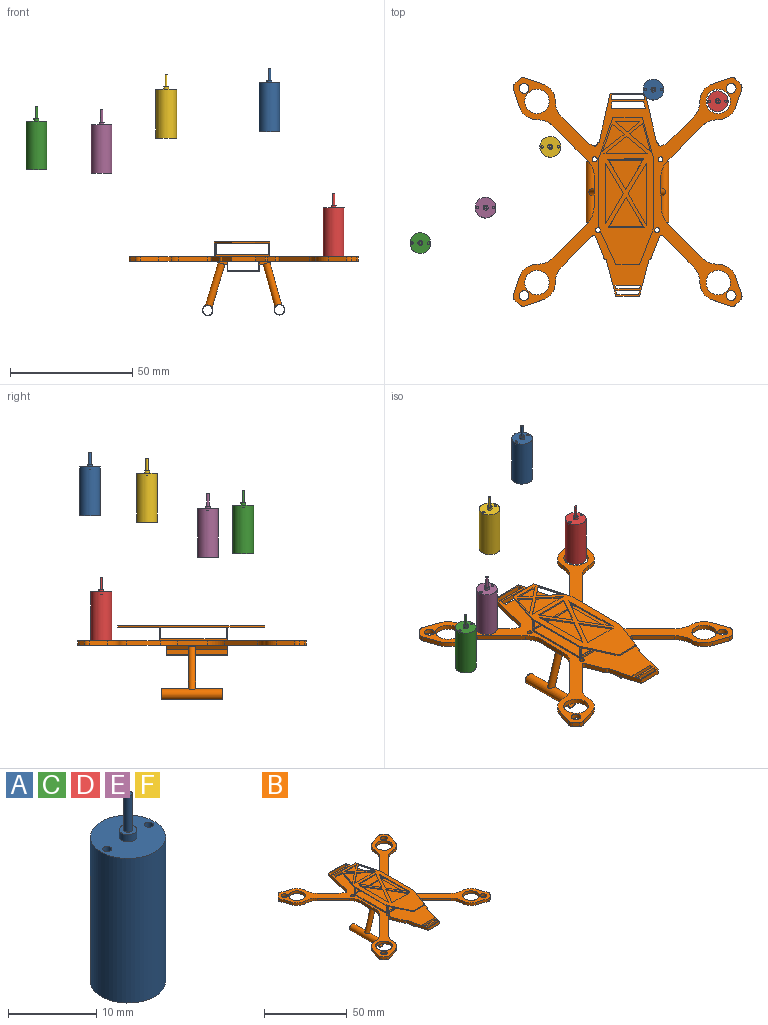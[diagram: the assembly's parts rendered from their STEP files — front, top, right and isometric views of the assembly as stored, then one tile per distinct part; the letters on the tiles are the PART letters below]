
ASSEMBLY  parts=6 mates=1
PART A: 11 faces, bbox 8.5x8.5x26 mm
  f0: plane 8.5x8.5mm, normal (0,0,1), area 52mm2, adj f1,f6,f7,f9
  f1: cylinder r=1mm len=2mm, axis (0,0,-1), area 6.3mm2, adj f0,f2
  f2: plane 2x2mm, normal (0,0,1), area 2.4mm2, adj f1,f3
  f3: cylinder r=0.5mm len=5mm, axis (0,0,-1), area 15.7mm2, adj f2,f4
  f4: plane 1x1mm, normal (0,0,1), area 0.8mm2, adj f3
  f5: plane 8.5x8.5mm, normal (0,0,-1), area 56.7mm2, adj f6
  f6: cylinder r=4.25mm len=20mm, axis (0,0,-1), area 534.1mm2, adj f0,f5
  f7: cylinder r=0.5mm len=1mm, axis (0,0,1), area 3.1mm2, adj f0,f8
  f8: plane 1x1mm, normal (0,0,1), area 0.8mm2, adj f7
  f9: cylinder r=0.5mm len=1mm, axis (0,0,1), area 3.1mm2, adj f0,f10
  f10: plane 1x1mm, normal (0,0,1), area 0.8mm2, adj f9
PART B: 207 faces, bbox 93.7x93.7x30.2 mm
  f0: plane 24.87x13.05mm, normal (0,0,-1), area 202.4mm2, adj f10,f122,f123,f124,f167,f168,f169,f170
  f1: plane 24.87x12.57mm, normal (0,0,1), area 190.7mm2, adj f10,f124,f125,f126,f167,f168,f169,f170
  f2: plane 60.16x22.71mm, normal (0,0,1), area 647.4mm2, adj f16,f18,f19,f20,f89,f103,f104,f105
  f3: plane 22.71x17.62mm, normal (0,0,-1), area 139.9mm2, adj f5,f18,f19,f20,f98,f99,f101,f103
  f4: plane 22.34x15.76mm, normal (0,0,-1), area 246.4mm2, adj f6,f16,f17,f21,f23,f105,f106,f143
  f5: plane 22.71x4.77mm, normal (0,-1,0), area 9.6mm2, adj f3,f7,f19,f20,f99,f100,f101,f102
  f6: plane 22.71x4.77mm, normal (0,1,0), area 9.6mm2, adj f4,f7,f19,f20,f21,f22,f23,f102
  f7: plane 26.78x22.71mm, normal (0,0,-1), area 259.4mm2, adj f5,f6,f19,f20,f143,f145,f146,f148
  f8: plane 93.73x93.73mm, normal (0,0,-1), area 2513.7mm2, adj f10,f11,f14,f15,f24,f25,f26,f27
  f9: plane 93.73x93.73mm, normal (0,0,1), area 2146.7mm2, adj f14,f15,f17,f19,f20,f24,f25,f26
  f10: plane 18.07x4mm, normal (0,-1,0), area 8.7mm2, adj f0,f1,f8,f11,f112,f122,f123,f125
  f11: plane 24.87x5.02mm, normal (-0.29,0,-0.96), area 123.4mm2, adj f8,f10,f13,f122,f124
  f12: cylinder r=1.5mm len=18.46mm, axis (-0.27,0,0.96), area 168.9mm2, adj f113,f117
  f13: cylinder r=1.5mm len=18.62mm, axis (0.29,0,0.96), area 170.6mm2, adj f11,f114
  f14: plane 14.44x2mm, normal (0,1,0), area 28.9mm2, adj f8,f9,f109,f110
  f15: plane 9.8x2mm, normal (0,-1,0), area 19.6mm2, adj f8,f9,f107,f108
  f16: plane 9.68x0.61mm, normal (0,-1,0), area 5.9mm2, adj f2,f4,f105,f106
  f17: plane 22.34x5.39mm, normal (0,-1,0), area 22.2mm2, adj f4,f9,f19,f21,f22,f23,f89
  f18: plane 12.03x0.61mm, normal (0,1,0), area 7.4mm2, adj f2,f3,f103,f104
  f19: plane 28.32x6mm, normal (1,0,0), area 41.4mm2, adj f2,f3,f5,f6,f7,f9,f17,f98
  f20: plane 28.07x6mm, normal (-1,0,0), area 40.6mm2, adj f2,f3,f5,f6,f7,f9,f89,f98
  f21: plane 4.58x0.76mm, normal (-1,0,0), area 3.5mm2, adj f4,f6,f17,f22
  f22: plane 21.4x0.76mm, normal (0,0,1), area 16.3mm2, adj f6,f17,f21,f23
  f23: plane 4.58x0.76mm, normal (1,0,0), area 3.5mm2, adj f4,f6,f17,f22
  f24: plane 7.46x2.53mm, normal (0.32,-0.95,0), area 15.8mm2, adj f8,f9,f25,f95
  f25: cylinder r=7.5mm len=7.1mm, axis (0,0,-1), area 18.7mm2, adj f8,f9,f24,f26
  f26: cylinder r=9.56mm len=6.75mm, axis (0,0,-1), area 15mm2, adj f8,f9,f25,f27
  f27: plane 12.22x12.22mm, normal (0.71,-0.71,0), area 34.6mm2, adj f8,f9,f26,f28
  f28: cylinder r=1mm len=2mm, axis (0,0,-1), area 4mm2, adj f8,f9,f27,f29
  f29: plane 8.48x3.23mm, normal (-0.93,-0.36,0), area 18.1mm2, adj f8,f9,f28,f30
  f30: cylinder r=1mm len=2mm, axis (0,0,-1), area 2.4mm2, adj f8,f9,f29,f107
  f31: cylinder r=1mm len=2mm, axis (0,0,-1), area 2.4mm2, adj f8,f9,f32,f108
  f32: plane 8.48x3.23mm, normal (0.93,-0.36,0), area 18.1mm2, adj f8,f9,f31,f33
  f33: cylinder r=1mm len=2mm, axis (0,0,-1), area 4mm2, adj f8,f9,f32,f34
  f34: plane 12.22x12.22mm, normal (-0.71,-0.71,0), area 34.6mm2, adj f8,f9,f33,f35
  f35: cylinder r=9.56mm len=6.75mm, axis (0,0,-1), area 15mm2, adj f8,f9,f34,f36
  f36: cylinder r=7.5mm len=7.1mm, axis (0,0,-1), area 18.7mm2, adj f8,f9,f35,f37
  f37: plane 7.46x2.53mm, normal (-0.32,-0.95,0), area 15.8mm2, adj f8,f9,f36,f38
  f38: cylinder r=2mm len=2.06mm, axis (0,0,-1), area 4.5mm2, adj f8,f9,f37,f39
  f39: plane 2.05x2.05mm, normal (0.71,-0.71,0), area 5.8mm2, adj f8,f9,f38,f40
  f40: cylinder r=2mm len=2.06mm, axis (0,0,-1), area 4.5mm2, adj f8,f9,f39,f41
  f41: plane 7.46x2.53mm, normal (0.95,0.32,0), area 15.8mm2, adj f8,f9,f40,f42
  f42: cylinder r=7.5mm len=7.1mm, axis (0,0,-1), area 18.7mm2, adj f8,f9,f41,f43
  f43: cylinder r=9.56mm len=6.75mm, axis (0,0,-1), area 15mm2, adj f8,f9,f42,f44
  f44: plane 13.69x13.69mm, normal (0.71,0.71,0), area 38.7mm2, adj f8,f9,f43,f45
  f45: cylinder r=10mm len=6.95mm, axis (0,0,-1), area 15.5mm2, adj f8,f9,f44,f46
  f46: plane 11.98x2mm, normal (1,0.01,0), area 24mm2, adj f8,f9,f45,f47
  f47: cylinder r=10mm len=7.2mm, axis (0,0,-1), area 16mm2, adj f8,f9,f46,f48
  f48: plane 13.85x13.85mm, normal (0.71,-0.71,0), area 39.2mm2, adj f8,f9,f47,f49
  f49: cylinder r=9.56mm len=6.75mm, axis (0,0,-1), area 15mm2, adj f8,f9,f48,f50
  f50: cylinder r=7.5mm len=7.1mm, axis (0,0,-1), area 18.7mm2, adj f8,f9,f49,f51
  f51: plane 7.46x2.53mm, normal (0.95,-0.32,0), area 15.8mm2, adj f8,f9,f50,f52
  f52: cylinder r=2mm len=2.06mm, axis (0,0,-1), area 4.5mm2, adj f8,f9,f51,f53
  f53: plane 2.05x2.05mm, normal (0.71,0.71,0), area 5.8mm2, adj f8,f9,f52,f54
  f54: cylinder r=2mm len=2.06mm, axis (0,0,-1), area 4.5mm2, adj f8,f9,f53,f55
  f55: plane 7.46x2.53mm, normal (-0.32,0.95,0), area 15.8mm2, adj f8,f9,f54,f56
  f56: cylinder r=7.5mm len=7.1mm, axis (0,0,-1), area 18.7mm2, adj f8,f9,f55,f57
  f57: cylinder r=9.56mm len=6.75mm, axis (0,0,-1), area 15mm2, adj f8,f9,f56,f58
  f58: plane 9.06x9.06mm, normal (-0.71,0.71,0), area 25.6mm2, adj f8,f9,f57,f59
  f59: cylinder r=10mm len=3.96mm, axis (0,0,-1), area 9.4mm2, adj f8,f9,f58,f60
  f60: cylinder r=1mm len=2mm, axis (0,0,-1), area 3.8mm2, adj f8,f9,f59,f61
  f61: cylinder r=0.78mm len=2mm, axis (0,0,-1), area 1.8mm2, adj f8,f9,f60,f109
  f62: cylinder r=0.78mm len=2mm, axis (0,0,-1), area 2.2mm2, adj f8,f9,f63,f110
  f63: cylinder r=1mm len=2mm, axis (0,0,-1), area 3.8mm2, adj f8,f9,f62,f64
  f64: cylinder r=10mm len=3.96mm, axis (0,0,-1), area 9.4mm2, adj f8,f9,f63,f65
  f65: plane 9.06x9.06mm, normal (0.71,0.71,0), area 25.6mm2, adj f8,f9,f64,f66
  f66: cylinder r=9.56mm len=6.75mm, axis (0,0,-1), area 15mm2, adj f8,f9,f65,f67
  f67: cylinder r=7.5mm len=7.1mm, axis (0,0,-1), area 18.7mm2, adj f8,f9,f66,f68
  f68: plane 7.46x2.53mm, normal (0.32,0.95,0), area 15.8mm2, adj f8,f9,f67,f69
  f69: cylinder r=2mm len=2.06mm, axis (0,0,-1), area 4.5mm2, adj f8,f9,f68,f70
  f70: plane 2.05x2.05mm, normal (-0.71,0.71,0), area 5.8mm2, adj f8,f9,f69,f71
  f71: cylinder r=2mm len=2.06mm, axis (0,0,-1), area 4.5mm2, adj f8,f9,f70,f72
  f72: plane 7.46x2.53mm, normal (-0.95,-0.32,0), area 15.8mm2, adj f8,f9,f71,f73
  f73: cylinder r=7.5mm len=7.1mm, axis (0,0,-1), area 18.7mm2, adj f8,f9,f72,f74
  f74: cylinder r=9.56mm len=6.75mm, axis (0,0,-1), area 15mm2, adj f8,f9,f73,f75
  f75: plane 13.85x13.85mm, normal (-0.71,-0.71,0), area 39.2mm2, adj f8,f9,f74,f76
  f76: cylinder r=10mm len=7.2mm, axis (0,0,-1), area 16mm2, adj f8,f9,f75,f77
  f77: plane 11.98x2mm, normal (-1,0.01,0), area 24mm2, adj f8,f9,f76,f78
  f78: cylinder r=10mm len=6.95mm, axis (0,0,-1), area 15.5mm2, adj f8,f9,f77,f79
  f79: plane 13.69x13.69mm, normal (-0.71,0.71,0), area 38.7mm2, adj f8,f9,f78,f80
  f80: cylinder r=9.56mm len=6.75mm, axis (0,0,-1), area 15mm2, adj f8,f9,f79,f81
  f81: cylinder r=7.5mm len=7.1mm, axis (0,0,-1), area 18.7mm2, adj f8,f9,f80,f82
  f82: plane 7.46x2.53mm, normal (-0.95,0.32,0), area 15.8mm2, adj f8,f9,f81,f83
  f83: cylinder r=2mm len=2.06mm, axis (0,0,-1), area 4.5mm2, adj f8,f9,f82,f84
  f84: plane 2.05x2.05mm, normal (-0.71,-0.71,0), area 5.8mm2, adj f8,f9,f83,f95
  f85: cylinder r=5mm len=10mm, axis (0,0,-1), area 62.8mm2, adj f8,f9
  f86: cylinder r=5mm len=10mm, axis (0,0,-1), area 62.8mm2, adj f8,f9
  f87: cylinder r=2mm len=4mm, axis (0,0,-1), area 25.1mm2, adj f8,f9
  f88: cylinder r=1mm len=2mm, axis (0,0,-1), area 12.6mm2, adj f8,f9
  f89: cylinder r=1mm len=8mm, axis (0,0,-1), area 14.9mm2, adj f2,f8,f9,f17,f20,f105
  f90: cylinder r=1mm len=2mm, axis (0,0,-1), area 12.6mm2, adj f8,f9
  f91: cylinder r=2mm len=4mm, axis (0,0,-1), area 25.1mm2, adj f8,f9
  f92: cylinder r=2mm len=4mm, axis (0,0,-1), area 25.1mm2, adj f8,f9
  f93: cylinder r=5mm len=10mm, axis (0,0,-1), area 62.8mm2, adj f8,f9
  f94: cylinder r=2mm len=4mm, axis (0,0,-1), area 25.1mm2, adj f8,f9
  f95: cylinder r=2mm len=2.06mm, axis (0,0,-1), area 4.5mm2, adj f8,f9,f24,f84
  f96: cylinder r=1mm len=2mm, axis (0,0,-1), area 12.6mm2, adj f8,f9
  f97: cylinder r=5mm len=10mm, axis (0,0,-1), area 62.8mm2, adj f8,f9
  f98: plane 22.71x5.39mm, normal (0,1,0), area 24.3mm2, adj f3,f9,f19,f20,f99,f100,f101
  f99: plane 4.58x0.62mm, normal (-1,0,0), area 2.8mm2, adj f3,f5,f98,f100
  f100: plane 21.4x0.62mm, normal (0,0,1), area 13.2mm2, adj f5,f98,f99,f101
  f101: plane 4.58x0.62mm, normal (1,0,0), area 2.8mm2, adj f3,f5,f98,f100
  f102: plane 26.78x22.71mm, normal (0,0,1), area 608.3mm2, adj f5,f6,f19,f20
  f103: plane 16.84x4.69mm, normal (0.96,0.27,0), area 10.7mm2, adj f2,f3,f18,f19
  f104: plane 16.98x6mm, normal (-0.94,0.33,0), area 11.1mm2, adj f2,f3,f18,f20
  f105: plane 15x6.85mm, normal (-0.91,-0.42,0), area 10.1mm2, adj f2,f4,f16,f89
  f106: plane 15x5.81mm, normal (0.93,-0.36,0), area 9.9mm2, adj f2,f4,f16,f19
  f107: plane 15x3.93mm, normal (-0.97,-0.25,0), area 31mm2, adj f8,f9,f15,f30
  f108: plane 15x3.89mm, normal (0.97,-0.25,0), area 31mm2, adj f8,f9,f15,f31
  f109: plane 20x4.56mm, normal (0.98,0.22,0), area 41mm2, adj f8,f9,f14,f61
  f110: plane 20x4.5mm, normal (-0.98,0.22,0), area 41mm2, adj f8,f9,f14,f62
  f111: plane 5.43x1.5mm, normal (0,-1,0), area 4.1mm2, adj f8,f112,f113
  f112: plane 1.5x0.12mm, normal (-1,0,0), area 0.2mm2, adj f8,f10,f111,f113
  f113: plane 24.99x5.43mm, normal (0.27,0,-0.96), area 133.8mm2, adj f8,f12,f111,f112,f123,f124
  f114: cylinder r=2.19mm len=25mm, axis (0,1,0), area 335.8mm2, adj f13,f115,f116
  f115: plane 4.37x4.37mm, normal (0,-1,0), area 2.4mm2, adj f114,f121
  f116: plane 4.37x4.37mm, normal (0,1,0), area 2.4mm2, adj f114,f121
  f117: cylinder r=2.19mm len=25mm, axis (0,1,0), area 335.7mm2, adj f12,f118,f119
  f118: plane 4.37x4.37mm, normal (0,-1,0), area 2.4mm2, adj f117,f120
  f119: plane 4.37x4.37mm, normal (0,1,0), area 2.4mm2, adj f117,f120
  f120: cylinder r=2mm len=25mm, axis (0,-1,0), area 314.8mm2, adj f118,f119
  f121: cylinder r=2mm len=25mm, axis (0,-1,0), area 314.1mm2, adj f115,f116
  f122: plane 24.87x2.5mm, normal (-1,0,0), area 62.2mm2, adj f0,f10,f11,f124
  f123: plane 24.87x2.5mm, normal (1,0,0), area 62.2mm2, adj f0,f10,f113,f124
  f124: plane 23.5x4mm, normal (0,1,0), area 12.8mm2, adj f0,f1,f8,f11,f113,f122,f123,f125
  f125: plane 24.87x3.76mm, normal (-1,0,0), area 93.4mm2, adj f1,f8,f10,f124
  f126: plane 24.87x3.76mm, normal (1,0,0), area 93.4mm2, adj f1,f8,f10,f124
  f127: plane 2.05x2mm, normal (0.98,-0.19,0), area 4.2mm2, adj f8,f9,f128,f130
  f128: plane 13.74x2mm, normal (0,1,0), area 27.5mm2, adj f8,f9,f127,f129
  f129: plane 2.05x2mm, normal (-0.98,-0.21,0), area 4.2mm2, adj f8,f9,f128,f130
  f130: plane 12.91x2mm, normal (0,-1,0), area 25.8mm2, adj f8,f9,f127,f129
  f131: plane 2.64x2mm, normal (0.99,-0.14,0), area 5.3mm2, adj f8,f9,f132,f134
  f132: plane 14.01x2mm, normal (0,1,0), area 28mm2, adj f8,f9,f131,f133
  f133: plane 2.64x2mm, normal (-0.97,-0.26,0), area 5.5mm2, adj f8,f9,f132,f134
  f134: plane 12.91x2mm, normal (0,-1,0), area 25.8mm2, adj f8,f9,f131,f133
  f135: plane 2x1.49mm, normal (-0.97,0.25,0), area 3.1mm2, adj f8,f9,f136,f138
  f136: plane 10.39x2mm, normal (0,-1,0), area 20.8mm2, adj f8,f9,f135,f137
  f137: plane 2x1.49mm, normal (0.97,0.25,0), area 3.1mm2, adj f8,f9,f136,f138
  f138: plane 9.61x2mm, normal (0,1,0), area 19.2mm2, adj f8,f9,f135,f137
  f139: plane 2x1.51mm, normal (-0.97,0.25,0), area 3.1mm2, adj f8,f9,f140,f142
  f140: plane 9.61x2mm, normal (0,-1,0), area 19.2mm2, adj f8,f9,f139,f141
  f141: plane 2x1.51mm, normal (0.97,0.25,0), area 3.1mm2, adj f8,f9,f140,f142
  f142: plane 8.83x2mm, normal (0,1,0), area 17.7mm2, adj f8,f9,f139,f141
  f143: plane 12.36x7.25mm, normal (0.86,-0.51,0), area 8.2mm2, adj f2,f4,f6,f7,f144,f145
  f144: plane 14.67x0.61mm, normal (0,1,0), area 9mm2, adj f2,f4,f143,f145
  f145: plane 12.44x7.42mm, normal (-0.86,-0.51,0), area 8.3mm2, adj f2,f4,f6,f7,f143,f144
  f146: plane 12.58x7.38mm, normal (-0.86,0.51,0), area 8.3mm2, adj f2,f3,f5,f7,f147,f148
  f147: plane 14.67x0.61mm, normal (0.01,-1,0), area 9mm2, adj f2,f3,f146,f148
  f148: plane 12.49x7.29mm, normal (0.86,0.5,0), area 8.2mm2, adj f2,f3,f5,f7,f146,f147
  f149: plane 12.6x7.39mm, normal (0.86,-0.51,0), area 8.3mm2, adj f2,f7,f150,f151
  f150: plane 12.93x7.55mm, normal (0.86,0.5,0), area 8.5mm2, adj f2,f7,f149,f151
  f151: plane 25.53x0.57mm, normal (-1,-0.01,0), area 14.5mm2, adj f2,f7,f149,f150
  f152: plane 12.36x7.25mm, normal (-0.86,0.51,0), area 8.1mm2, adj f2,f7,f153,f154
  f153: plane 12.4x7.4mm, normal (-0.86,-0.51,0), area 8.2mm2, adj f2,f7,f152,f154
  f154: plane 24.77x0.57mm, normal (1,0.01,0), area 14.1mm2, adj f2,f7,f152,f153
  f155: plane 4.93x4.12mm, normal (-0.64,-0.77,0), area 3.9mm2, adj f2,f3,f156,f157
  f156: plane 11.08x3.91mm, normal (0.94,-0.33,0), area 7.2mm2, adj f2,f3,f155,f157
  f157: plane 8.84x6.96mm, normal (-0.62,0.79,0), area 6.9mm2, adj f2,f3,f155,f156
  f158: plane 5.23x4.12mm, normal (-0.62,0.79,0), area 4.1mm2, adj f2,f3,f159,f160
  f159: plane 10.15x0.61mm, normal (0,-1,0), area 6.2mm2, adj f2,f3,f158,f160
  f160: plane 4.92x4.12mm, normal (0.64,0.77,0), area 3.9mm2, adj f2,f3,f158,f159
  f161: plane 8.65x7.24mm, normal (-0.64,-0.77,0), area 6.9mm2, adj f2,f3,f162,f163
  f162: plane 9.19x7.24mm, normal (0.62,-0.79,0), area 7.2mm2, adj f2,f3,f161,f163
  f163: plane 17.85x0.61mm, normal (0,1,0), area 11mm2, adj f2,f3,f161,f162
  f164: plane 5.44x4.28mm, normal (0.62,-0.79,0), area 4.3mm2, adj f2,f3,f165,f166
  f165: plane 8.64x7.23mm, normal (0.64,0.77,0), area 6.9mm2, adj f2,f3,f164,f166
  f166: plane 11.51x3.2mm, normal (-0.96,-0.27,0), area 7.3mm2, adj f2,f3,f164,f165
  f167: plane 3.03x0.24mm, normal (1,0,0), area 0.7mm2, adj f0,f1,f168,f170
  f168: plane 4.2x0.24mm, normal (0,-1,0), area 1mm2, adj f0,f1,f167,f169
  f169: plane 3.03x0.24mm, normal (-1,0,0), area 0.7mm2, adj f0,f1,f168,f170
  f170: plane 4.2x0.24mm, normal (0,1,0), area 1mm2, adj f0,f1,f167,f169
  f171: plane 3.85x0.24mm, normal (0,1,0), area 0.9mm2, adj f0,f1,f172,f174
  f172: plane 3.07x0.24mm, normal (1,0,0), area 0.7mm2, adj f0,f1,f171,f173
  f173: plane 3.85x0.24mm, normal (0,-1,0), area 0.9mm2, adj f0,f1,f172,f174
  f174: plane 3.07x0.24mm, normal (-1,0,0), area 0.7mm2, adj f0,f1,f171,f173
  f175: plane 4.2x0.24mm, normal (0,1,0), area 1mm2, adj f0,f1,f176,f178
  f176: plane 3.01x0.24mm, normal (1,0,0), area 0.7mm2, adj f0,f1,f175,f177
  f177: plane 4.2x0.24mm, normal (0,-1,0), area 1mm2, adj f0,f1,f176,f178
  f178: plane 3.01x0.24mm, normal (-1,0,0), area 0.7mm2, adj f0,f1,f175,f177
  f179: plane 3.85x0.24mm, normal (0,1,0), area 0.9mm2, adj f0,f1,f180,f182
  f180: plane 3.01x0.24mm, normal (1,0,0), area 0.7mm2, adj f0,f1,f179,f181
  f181: plane 3.85x0.24mm, normal (0,-1,0), area 0.9mm2, adj f0,f1,f180,f182
  f182: plane 3.01x0.24mm, normal (-1,0,0), area 0.7mm2, adj f0,f1,f179,f181
  f183: plane 4.2x0.24mm, normal (0,1,0), area 1mm2, adj f0,f1,f184,f186
  f184: plane 3.01x0.24mm, normal (1,0,0), area 0.7mm2, adj f0,f1,f183,f185
  f185: plane 4.2x0.24mm, normal (0,-1,0), area 1mm2, adj f0,f1,f184,f186
  f186: plane 3.01x0.24mm, normal (-1,0,0), area 0.7mm2, adj f0,f1,f183,f185
  f187: plane 3.85x0.24mm, normal (0,1,0), area 0.9mm2, adj f0,f1,f188,f190
  f188: plane 3.03x0.24mm, normal (1,0,0), area 0.7mm2, adj f0,f1,f187,f189
  f189: plane 3.85x0.24mm, normal (0,-1,0), area 0.9mm2, adj f0,f1,f188,f190
  f190: plane 3.03x0.24mm, normal (-1,0,0), area 0.7mm2, adj f0,f1,f187,f189
  f191: plane 4.2x0.24mm, normal (0,1,0), area 1mm2, adj f0,f1,f192,f194
  f192: plane 3.07x0.24mm, normal (1,0,0), area 0.7mm2, adj f0,f1,f191,f193
  f193: plane 4.2x0.24mm, normal (0,-1,0), area 1mm2, adj f0,f1,f192,f194
  f194: plane 3.07x0.24mm, normal (-1,0,0), area 0.7mm2, adj f0,f1,f191,f193
  f195: plane 3.85x0.24mm, normal (0,1,0), area 0.9mm2, adj f0,f1,f196,f198
  f196: plane 3.03x0.24mm, normal (1,0,0), area 0.7mm2, adj f0,f1,f195,f197
  f197: plane 3.85x0.24mm, normal (0,-1,0), area 0.9mm2, adj f0,f1,f196,f198
  f198: plane 3.03x0.24mm, normal (-1,0,0), area 0.7mm2, adj f0,f1,f195,f197
  f199: plane 4.2x0.24mm, normal (0,1,0), area 1mm2, adj f0,f1,f200,f202
  f200: plane 3.03x0.24mm, normal (1,0,0), area 0.7mm2, adj f0,f1,f199,f201
  f201: plane 4.2x0.24mm, normal (0,-1,0), area 1mm2, adj f0,f1,f200,f202
  f202: plane 3.03x0.24mm, normal (-1,0,0), area 0.7mm2, adj f0,f1,f199,f201
  f203: plane 3.85x0.24mm, normal (0,1,0), area 0.9mm2, adj f0,f1,f204,f206
  f204: plane 3.01x0.24mm, normal (1,0,0), area 0.7mm2, adj f0,f1,f203,f205
  f205: plane 3.85x0.24mm, normal (0,-1,0), area 0.9mm2, adj f0,f1,f204,f206
  f206: plane 3.01x0.24mm, normal (-1,0,0), area 0.7mm2, adj f0,f1,f203,f205
PART C: same geometry as A
PART D: same geometry as A
PART E: same geometry as A
PART F: same geometry as A
PLACE A t=(30.67,68.65,75.42)mm
PLACE B t=(19.7,26.84,14.7)mm
PLACE C t=(-64.79,5.83,59.8)mm
PLACE D t=(57.01,63.97,24.31)mm
PLACE E t=(-38.06,20.34,58.41)mm
PLACE F t=(-11.59,45.23,72.82)mm
MATE pin_slot D.f1 <-> B.f50  axis (0,0,-1) through (56.62,63.97,16.7)mm
